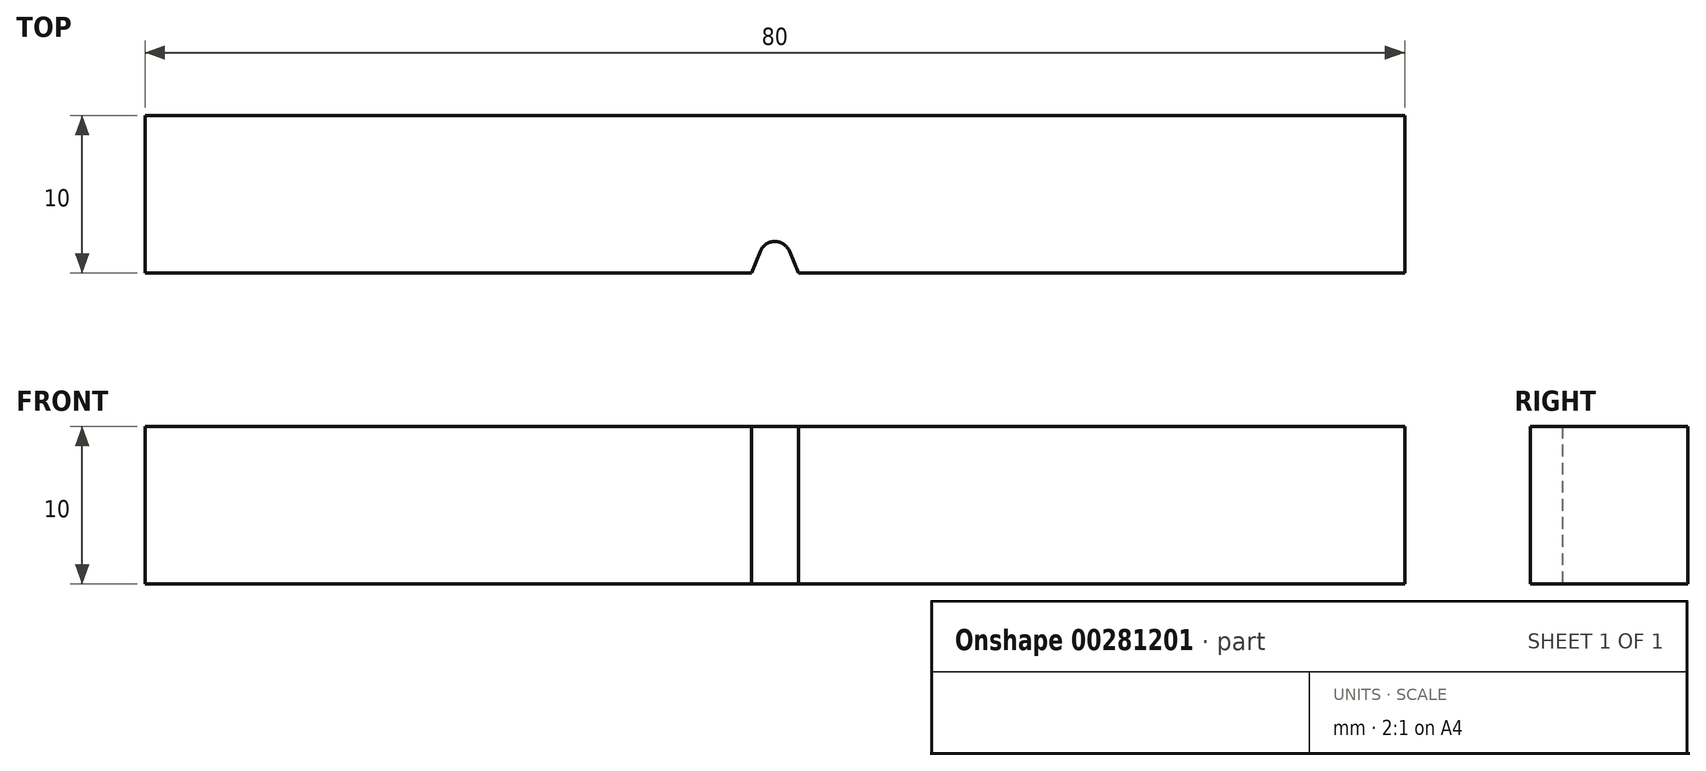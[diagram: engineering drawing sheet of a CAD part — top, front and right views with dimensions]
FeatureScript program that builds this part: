
annotation { "Feature Type Name" : "Feature", "Feature Type Description" : "" }
export const myFeature = defineFeature(function(context is Context, id is Id, definition is map)
    precondition{}
    {
        {
            var Q0;
            Q0=qCreatedBy(makeId("Top.planeOp"),FACE);
            var sketch = newSketch(context, id + "F0", { "sketchPlane" : qUnion([Q0])});
            skLineSegment(sketch, "E0.bottom", {"start": v(-40, 5) * mm, "end": v(40, 5) * mm});
            skLineSegment(sketch, "E0.top", {"start": v(-40, -5) * mm, "end": v(40, -5) * mm});
            skLineSegment(sketch, "E0.left", {"start": v(-40, 5) * mm, "end": v(-40, -5) * mm});
            skLineSegment(sketch, "E0.right", {"start": v(40, 5) * mm, "end": v(40, -5) * mm});
            skPoint(sketch, "E0.middle", {"position": v(0, 0) * mm});
            skLineSegment(sketch, "E1", {"start": v(-1.5, -5) * mm, "end": v(-0.92, -3.62) * mm});
            skLineSegment(sketch, "E2", {"start": v(0.92, -3.62) * mm, "end": v(1.5, -5) * mm});
            skPoint(sketch, "E3.visualSharp", {"position": v(0, -1.39) * mm});
            skArc(sketch, "E3.filletArc", {"start": v(0.92, -3.62) * mm, "mid": v(0, -3) * mm, "end": v(-0.92, -3.62) * mm});
            skPoint(sketch, "E4", {"position": v(0, -3) * mm});
            skSolve(sketch);
        }
        {
            var Q0;
            Q0=makeQuery(id+"F0.imprint","IMPRINT",FACE,{"disambiguationData":[TD([[makeQuery(id+"F0.imprint","IMPRINT",EDGE,{"derivedFrom":sQuery(id+"F0.wireOp",EDGE,"E0.bottom")}),-1.0]])]});
            extrude(context, id + "F1", {"entities" : qUnion([Q0]), "depth" : 10 * mm, "offsetDistance" : 25 * mm});
        }
    });
